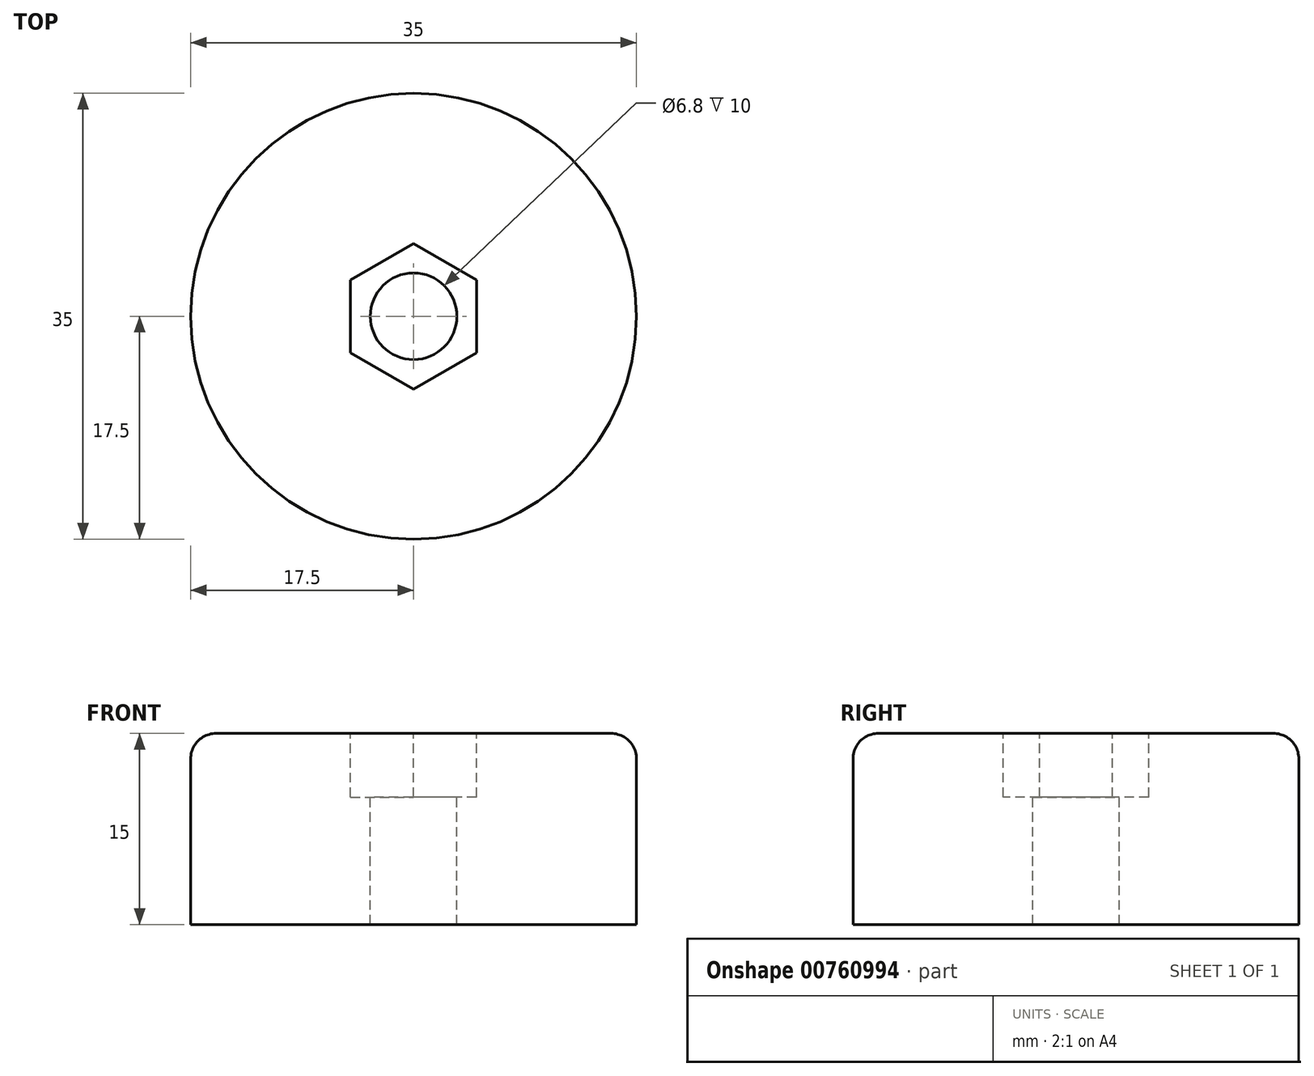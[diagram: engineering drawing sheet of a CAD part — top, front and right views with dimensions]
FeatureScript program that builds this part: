
annotation { "Feature Type Name" : "Feature", "Feature Type Description" : "" }
export const myFeature = defineFeature(function(context is Context, id is Id, definition is map)
    precondition{}
    {
        {
            var Q0;
            Q0=qCreatedBy(makeId("Top.planeOp"),FACE);
            var sketch = newSketch(context, id + "F0", { "sketchPlane" : qUnion([Q0])});
            skCircle(sketch, "E0", {"center": v(0, 0) * mm, "radius": 17.5 * mm});
            skSolve(sketch);
        }
        {
            var Q0;
            Q0=makeQuery(id+"F0.imprint","IMPRINT",FACE,{"disambiguationData":[TD([[makeQuery(id+"F0.imprint","IMPRINT",EDGE,{"derivedFrom":sQuery(id+"F0.wireOp",EDGE,"E0")}),1.0]])]});
            extrude(context, id + "F1", {"entities" : qUnion([Q0]), "depth" : 15 * mm, "offsetDistance" : 25 * mm});
        }
        {
            var Q0;
            Q0=makeQuery(id+"F1.opExtrude","CAP_FACE",FACE,{"disambiguationData":[OSD([sQuery(id+"F0.wireOp",EDGE,"E0")])],"isStart":false});
            var sketch = newSketch(context, id + "F2", { "sketchPlane" : qUnion([Q0])});
            skCircle(sketch, "E1.cCircle", {"center": v(0, 0) * mm, "radius": 4.95 * mm, "construction": true});
            skLineSegment(sketch, "E1.0", {"start": v(4.95, -2.86) * mm, "end": v(0, -5.72) * mm});
            skLineSegment(sketch, "E1.1", {"start": v(0, -5.72) * mm, "end": v(-4.95, -2.86) * mm});
            skLineSegment(sketch, "E1.2", {"start": v(-4.95, -2.86) * mm, "end": v(-4.95, 2.86) * mm});
            skLineSegment(sketch, "E1.3", {"start": v(-4.95, 2.86) * mm, "end": v(0, 5.72) * mm});
            skLineSegment(sketch, "E1.4", {"start": v(0, 5.72) * mm, "end": v(4.95, 2.86) * mm});
            skLineSegment(sketch, "E1.5", {"start": v(4.95, 2.86) * mm, "end": v(4.95, -2.86) * mm});
            skPoint(sketch, "E1.0.midPoint", {"position": v(2.47, -4.29) * mm});
            skSolve(sketch);
        }
        {
            var Q0;
            Q0=makeQuery(id+"F2.imprint","IMPRINT",FACE,{"disambiguationData":[TD([[makeQuery(id+"F2.imprint","IMPRINT",EDGE,{"derivedFrom":sQuery(id+"F2.wireOp",EDGE,"E1.0")}),-1.0]])]});
            extrude(context, id + "F3", {"entities" : qUnion([Q0]), "operationType" : NewBodyOperationType.REMOVE, "oppositeDirection" : true, "depth" : 5 * mm, "offsetDistance" : 25 * mm});
        }
        {
            var Q0;
            Q0=makeQuery(id+"F1.opExtrude","CAP_EDGE",EDGE,{"disambiguationData":[OSD([sQuery(id+"F0.wireOp",EDGE,"E0")])],"isStart":false});
            fillet(context, id + "F4", {"entities" : qUnion([Q0]), "radius" : 2 * mm, "tangentPropagation" : true, "allowEdgeOverflow" : false});
        }
        {
            var Q0;
            Q0=makeQuery(id+"F3.boolean.opBoolean","COPY",FACE,{"derivedFrom":makeQuery(id+"F3.opExtrude","CAP_FACE",FACE,{"disambiguationData":[OSD([sQuery(id+"F2.wireOp",EDGE,"E1.0"),sQuery(id+"F2.wireOp",EDGE,"E1.1"),sQuery(id+"F2.wireOp",EDGE,"E1.2"),sQuery(id+"F2.wireOp",EDGE,"E1.3"),sQuery(id+"F2.wireOp",EDGE,"E1.4"),sQuery(id+"F2.wireOp",EDGE,"E1.5")])],"isStart":false})});
            var sketch = newSketch(context, id + "F5", { "sketchPlane" : qUnion([Q0])});
            skCircle(sketch, "E2", {"center": v(0, 0) * mm, "radius": 3.4 * mm});
            skSolve(sketch);
        }
        {
            var Q0;
            Q0=makeQuery(id+"F5.imprint","IMPRINT",FACE,{"disambiguationData":[TD([[makeQuery(id+"F5.imprint","IMPRINT",EDGE,{"derivedFrom":sQuery(id+"F5.wireOp",EDGE,"E2")}),1.0]])]});
            extrude(context, id + "F6", {"entities" : qUnion([Q0]), "operationType" : NewBodyOperationType.REMOVE, "endBound" : BoundingType.THROUGH_ALL, "oppositeDirection" : true, "depth" : 25 * mm, "offsetDistance" : 25 * mm});
        }
    });
